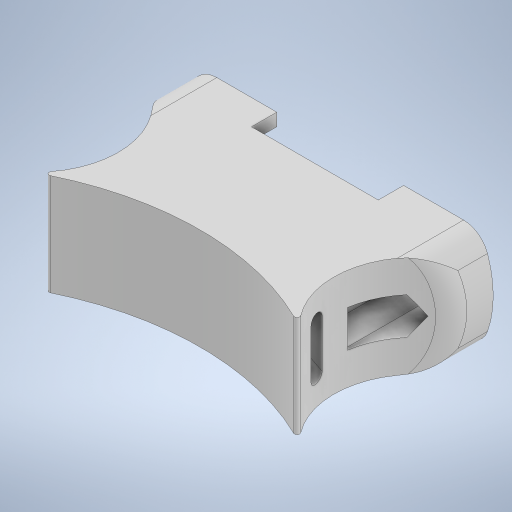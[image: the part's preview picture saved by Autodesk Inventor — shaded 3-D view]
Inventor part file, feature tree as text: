
AUTODESK INVENTOR PART (.ipt)
format: ipt  version: 2023 (Build 270158000, 158)  size: 455,680 bytes
history: native  units: mm
features: projected_geometry x9, extrude x8, sketch x8, fillet x3, other x2
ambient origin geometry x8: Origin, YZ Plane, XZ Plane, XY Plane, X Axis, Y Axis, Z Axis, Center Point
bodies: Body1 (feature_tree)
feature tree (30):
  other  "Těleso1"
  extrude  "Vysunutí1"  Depth=35.0mm
  extrude  "Vysunutí2"  Depth=20.0mm
  extrude  "Vysunutí3"  Depth=10.0mm TaperAngle=0.0deg
  extrude  "Vysunutí4"  Depth=15.0mm
  extrude  "Vysunutí5"  Depth=30.0mm
  other  "Rotace1"
  sketch  "Náčrt10"
  extrude  "Vysunutí9"  Depth=7.5mm TaperAngle=0.0deg
  extrude  "Vysunutí10"  Depth=5.0mm
  extrude  "Vysunutí11"  Depth=25.0mm
  fillet  "Zaoblení6"  [1 undecoded]
  fillet  "Zaoblení7"  Radius=20.0mm
  fillet  "Zaoblení9"  Radius=5.0mm
  sketch  "Náčrt1"
  sketch  "Náčrt2"
  projected_geometry  "Promítnutá smyčka1"
  sketch  "Náčrt3"
  projected_geometry  "Promítnutá smyčka2"
  sketch  "Náčrt4"
  projected_geometry  "Promítnutá smyčka3"
  projected_geometry  "Promítnutá smyčka4"
  sketch  "Náčrt6"
  projected_geometry  "Promítnutá smyčka8"
  sketch  "Náčrt7"
  projected_geometry  "Promítnutá smyčka11"
  projected_geometry  "Promítnutá smyčka12"
  sketch  "Náčrt11"
  projected_geometry  "Promítnutá smyčka13"
  projected_geometry  "Promítnutá smyčka14"
note: 1 required parameter value undecoded (feature->parameter linkage not recoverable at this tier; creation-order binding heuristic only, values carry confidence <= 0.55)
